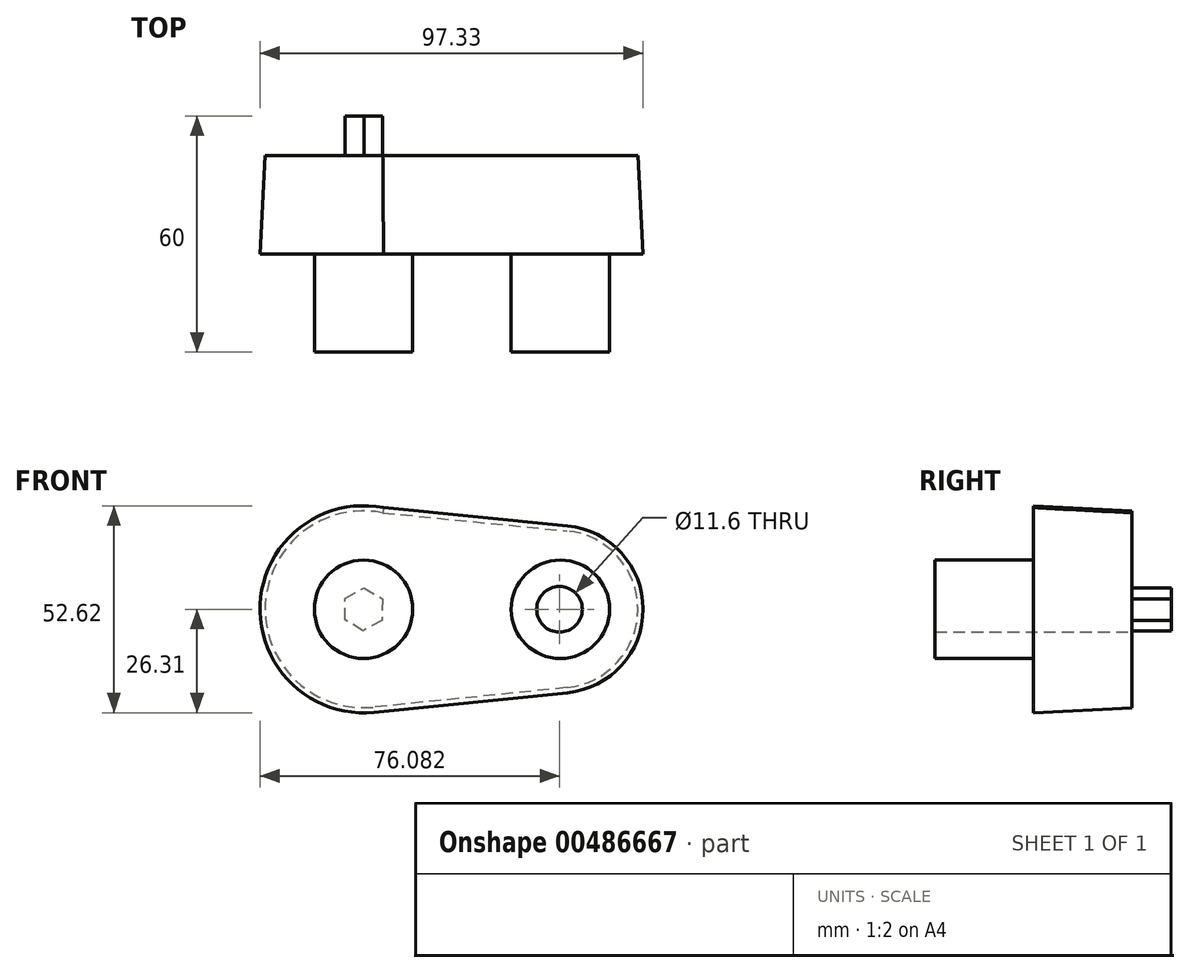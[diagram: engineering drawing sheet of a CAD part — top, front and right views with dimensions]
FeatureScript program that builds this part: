
annotation { "Feature Type Name" : "Feature", "Feature Type Description" : "" }
export const myFeature = defineFeature(function(context is Context, id is Id, definition is map)
    precondition{}
    {
        {
            var Q0;
            Q0=qCreatedBy(makeId("Front.planeOp"),FACE);
            var sketch = newSketch(context, id + "F0", { "sketchPlane" : qUnion([Q0])});
            skCircle(sketch, "E0", {"center": v(0, 0) * mm, "radius": 25 * mm});
            skCircle(sketch, "E1", {"center": v(49.7, 0) * mm, "radius": 20 * mm});
            skLineSegment(sketch, "E2", {"start": v(0, 25) * mm, "end": v(51.67, 19.9) * mm});
            skLineSegment(sketch, "E3", {"start": v(2.51, -24.87) * mm, "end": v(51.72, -19.9) * mm});
            skSolve(sketch);
        }
        {
            var Q0;
            Q0 = qSketchRegion(id + "F0", true);
            var Q1;
            Q1 = qSketchRegion(id + "F2", true);
            extrude(context, id + "F1", {"entities" : qUnion([Q0, Q1]), "depth" : 25 * mm, "hasDraft" : true, "draftAngle" : 3 * degree});
        }
        {
            var Q0;
            Q0=qCreatedBy(makeId("Front.planeOp"),FACE);
            var sketch = newSketch(context, id + "F2", { "sketchPlane" : qUnion([Q0])});
            skCircle(sketch, "E4", {"center": v(0, 0) * mm, "radius": 12.5 * mm});
            skCircle(sketch, "E5", {"center": v(50, 0) * mm, "radius": 12.5 * mm});
            skSolve(sketch);
        }
        {
            var Q0;
            Q0 = qSketchRegion(id + "F2", true);
            extrude(context, id + "F3", {"entities" : qUnion([Q0]), "operationType" : NewBodyOperationType.ADD, "depth" : 50 * mm});
        }
        {
            var Q0;
            Q0=qCreatedBy(makeId("Front.planeOp"),FACE);
            var sketch = newSketch(context, id + "F4", { "sketchPlane" : qUnion([Q0])});
            skCircle(sketch, "E6.cCircle", {"center": v(0, 0) * mm, "radius": 4.62 * mm, "construction": true});
            skLineSegment(sketch, "E6.0", {"start": v(2.86, -3.63) * mm, "end": v(-4.57, -0.66) * mm});
            skLineSegment(sketch, "E6.1", {"start": v(-4.57, -0.66) * mm, "end": v(1.72, 4.29) * mm});
            skLineSegment(sketch, "E6.2", {"start": v(1.72, 4.29) * mm, "end": v(2.86, -3.63) * mm});
            skCircle(sketch, "E7", {"center": v(49.77, 0) * mm, "radius": 5.8 * mm});
            skSolve(sketch);
        }
        {
            var Q0;
            Q0=makeQuery(id+"F4.imprint","IMPRINT",FACE,{"disambiguationData":[TD([[makeQuery(id+"F4.imprint","IMPRINT",EDGE,{"derivedFrom":sQuery(id+"F4.wireOp",EDGE,"E7")}),1.0]])]});
            extrude(context, id + "F5", {"entities" : qUnion([Q0]), "operationType" : NewBodyOperationType.REMOVE, "depth" : 50 * mm});
        }
        {
            var Q0;
            Q0=qCreatedBy(makeId("Front.planeOp"),FACE);
            var sketch = newSketch(context, id + "F6", { "sketchPlane" : qUnion([Q0])});
            skCircle(sketch, "E8.cCircle", {"center": v(0, 0) * mm, "radius": 5.45 * mm, "construction": true});
            skLineSegment(sketch, "E8.0", {"start": v(4.68, -2.8) * mm, "end": v(-0.08, -5.45) * mm});
            skLineSegment(sketch, "E8.1", {"start": v(-0.08, -5.45) * mm, "end": v(-4.76, -2.65) * mm});
            skLineSegment(sketch, "E8.2", {"start": v(-4.76, -2.65) * mm, "end": v(-4.68, 2.8) * mm});
            skLineSegment(sketch, "E8.3", {"start": v(-4.68, 2.8) * mm, "end": v(0.08, 5.45) * mm});
            skLineSegment(sketch, "E8.4", {"start": v(0.08, 5.45) * mm, "end": v(4.76, 2.65) * mm});
            skLineSegment(sketch, "E8.5", {"start": v(4.76, 2.65) * mm, "end": v(4.68, -2.8) * mm});
            skSolve(sketch);
        }
        {
            var Q0;
            Q0=makeQuery(id+"F6.imprint","IMPRINT",FACE,{"disambiguationData":[TD([[makeQuery(id+"F6.imprint","IMPRINT",EDGE,{"derivedFrom":sQuery(id+"F6.wireOp",EDGE,"E8.0")}),-1.0]])]});
            var Q1;
            Q1 = qBodyType(qCreatedBy(id + "F6" ,EDGE), BodyType.WIRE);
            var Q2;
            Q2=sQuery(id+"F6.wireOp",EDGE,"E8.0");
            var Q3;
            Q3=sQuery(id+"F6.wireOp",EDGE,"E8.3");
            var Q4;
            Q4=sQuery(id+"F6.wireOp",EDGE,"E8.2");
            var Q5;
            Q5=sQuery(id+"F6.wireOp",EDGE,"E8.5");
            var Q6;
            Q6=sQuery(id+"F6.wireOp",EDGE,"E8.4");
            var Q7;
            Q7=sQuery(id+"F6.wireOp",EDGE,"E8.1");
            extrude(context, id + "F7", {"entities" : qUnion([Q0]), "operationType" : NewBodyOperationType.ADD, "surfaceEntities" : qUnion([Q1, Q2, Q3, Q4, Q5, Q6, Q7]), "oppositeDirection" : true, "depth" : 10 * mm});
        }
    });
